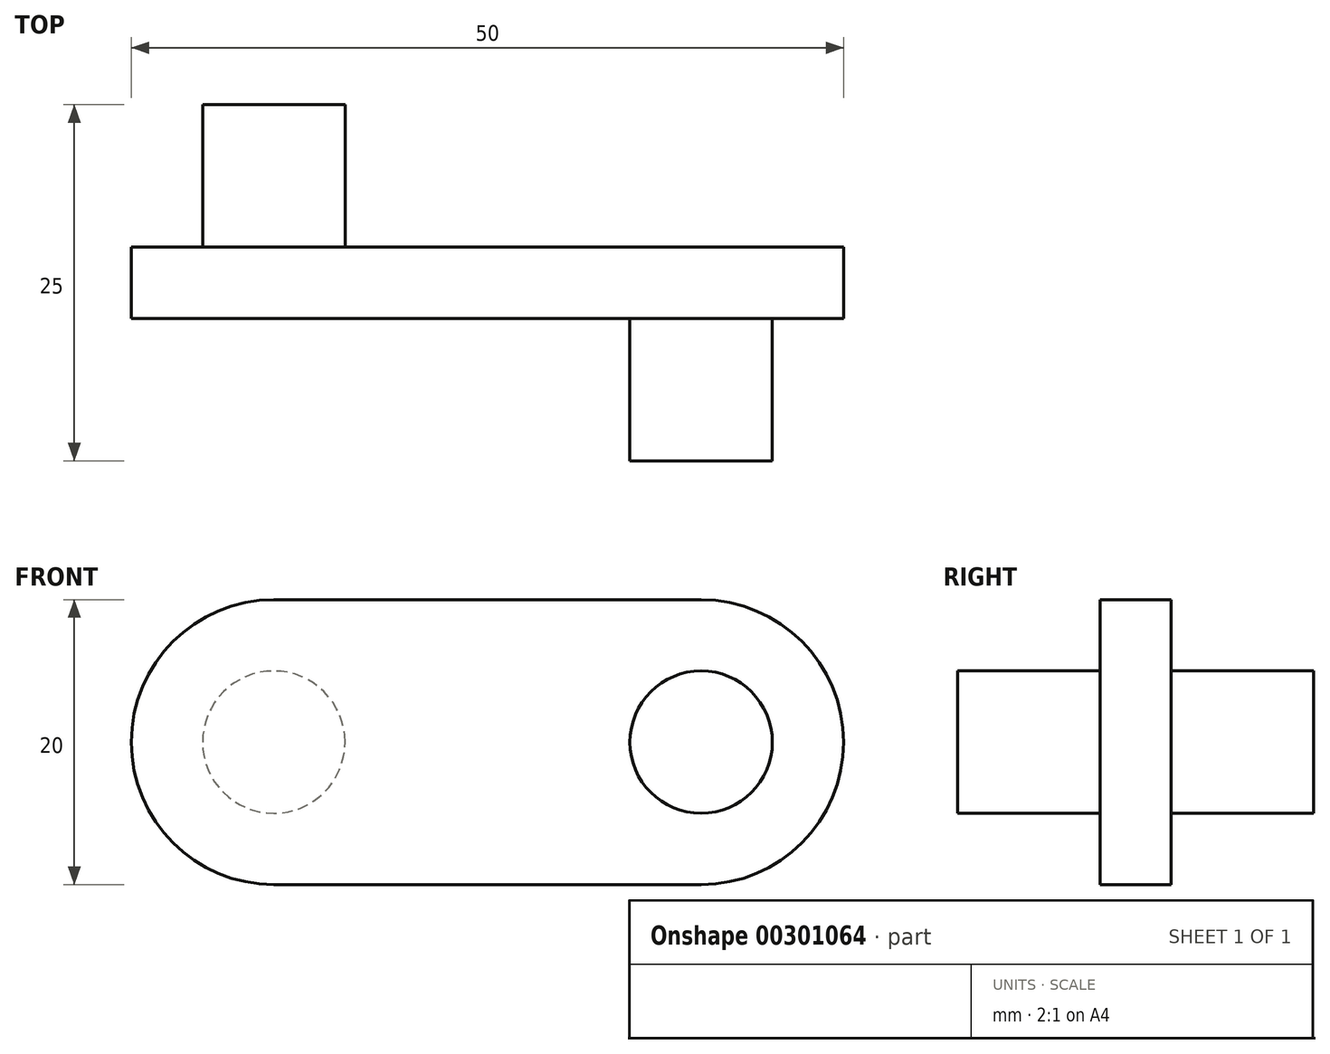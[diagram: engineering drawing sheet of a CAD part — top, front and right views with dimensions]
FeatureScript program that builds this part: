
annotation { "Feature Type Name" : "Feature", "Feature Type Description" : "" }
export const myFeature = defineFeature(function(context is Context, id is Id, definition is map)
    precondition{}
    {
        {
            var Q0;
            Q0=qCreatedBy(makeId("Front.planeOp"),FACE);
            var sketch = newSketch(context, id + "F0", { "sketchPlane" : qUnion([Q0])});
            skLineSegment(sketch, "E0.bottom", {"start": v(0, 0) * mm, "end": v(30, 0) * mm});
            skLineSegment(sketch, "E0.top", {"start": v(0, 20) * mm, "end": v(30, 20) * mm});
            skPoint(sketch, "E1", {"position": v(0, 10) * mm});
            skArc(sketch, "E2", {"start": v(0, 20) * mm, "mid": v(-7.07, 17.07) * mm, "end": v(-10, 10) * mm});
            skArc(sketch, "E3", {"start": v(-10, 10) * mm, "mid": v(-7.07, 2.93) * mm, "end": v(0, 0) * mm});
            skArc(sketch, "E4", {"start": v(30, 20) * mm, "mid": v(37.07, 17.07) * mm, "end": v(40, 10) * mm});
            skArc(sketch, "E5", {"start": v(40, 10) * mm, "mid": v(37.07, 2.93) * mm, "end": v(30, 0) * mm});
            skSolve(sketch);
        }
        {
            var Q0;
            Q0=makeQuery(id+"F0.imprint","IMPRINT",FACE,{"disambiguationData":[TD([[makeQuery(id+"F0.imprint","IMPRINT",EDGE,{"derivedFrom":sQuery(id+"F0.wireOp",EDGE,"E0.bottom")}),1.0]])]});
            var Q1;
            Q1=makeQuery(id+"F0.imprint","IMPRINT",FACE,{"disambiguationData":[TD([[makeQuery(id+"F0.imprint","IMPRINT",EDGE,{"derivedFrom":sQuery(id+"F0.wireOp",EDGE,"P8jOzeop-yWcu-rwv5-fKxV-WPVjlxbEkspA")}),1.0]])]});
            extrude(context, id + "F1", {"entities" : qUnion([Q0, Q1]), "depth" : 5 * mm});
        }
        {
            var Q0;
            Q0=makeQuery(id+"F1.opExtrude","CAP_FACE",FACE,{"disambiguationData":[OSD([sQuery(id+"F0.wireOp",EDGE,"E0.bottom"),sQuery(id+"F0.wireOp",EDGE,"E0.top"),sQuery(id+"F0.wireOp",EDGE,"E2"),sQuery(id+"F0.wireOp",EDGE,"E3"),sQuery(id+"F0.wireOp",EDGE,"E4"),sQuery(id+"F0.wireOp",EDGE,"E5")])],"isStart":false});
            var sketch = newSketch(context, id + "F2", { "sketchPlane" : qUnion([Q0])});
            skCircle(sketch, "E6", {"center": v(30, 10) * mm, "radius": 5 * mm});
            skSolve(sketch);
        }
        {
            var Q0;
            Q0 = qSketchRegion(id + "F2", true);
            extrude(context, id + "F3", {"entities" : qUnion([Q0]), "operationType" : NewBodyOperationType.ADD, "depth" : 10 * mm});
        }
        {
            var Q0;
            Q0=makeQuery(id+"F1.opExtrude","CAP_FACE",FACE,{"disambiguationData":[OSD([sQuery(id+"F0.wireOp",EDGE,"E0.bottom"),sQuery(id+"F0.wireOp",EDGE,"E0.top"),sQuery(id+"F0.wireOp",EDGE,"E2"),sQuery(id+"F0.wireOp",EDGE,"E3"),sQuery(id+"F0.wireOp",EDGE,"E4"),sQuery(id+"F0.wireOp",EDGE,"E5")])],"isStart":true});
            var sketch = newSketch(context, id + "F4", { "sketchPlane" : qUnion([Q0])});
            skCircle(sketch, "E7", {"center": v(0, 10) * mm, "radius": 5 * mm});
            skSolve(sketch);
        }
        {
            var Q0;
            Q0 = qSketchRegion(id + "F4", true);
            extrude(context, id + "F5", {"entities" : qUnion([Q0]), "operationType" : NewBodyOperationType.ADD, "depth" : 10 * mm});
        }
    });
